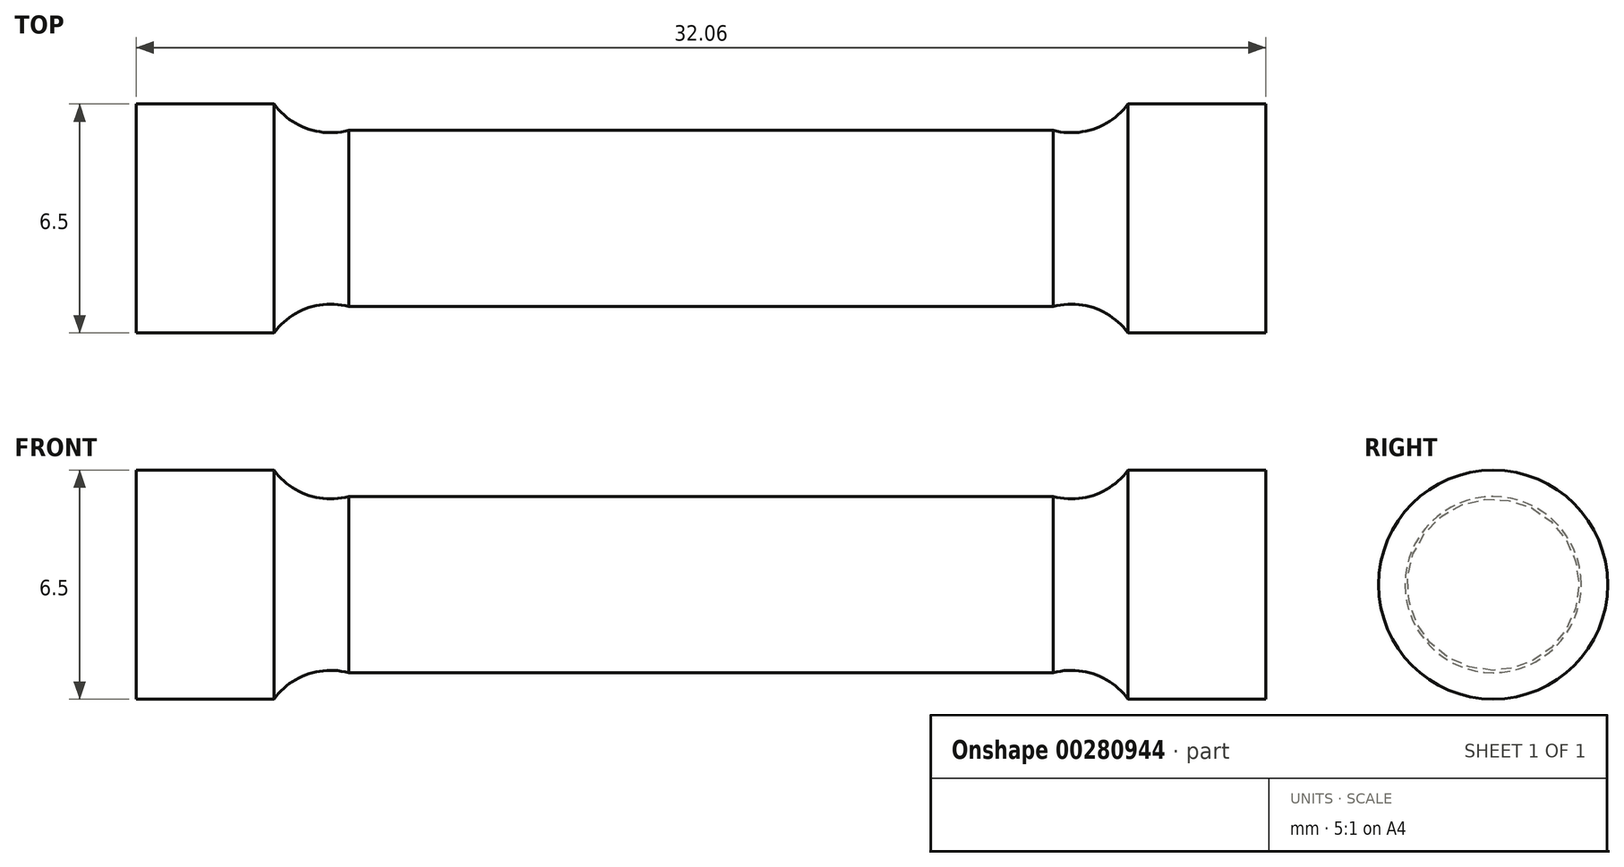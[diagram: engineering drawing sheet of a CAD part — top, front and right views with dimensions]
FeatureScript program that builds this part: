
annotation { "Feature Type Name" : "Feature", "Feature Type Description" : "" }
export const myFeature = defineFeature(function(context is Context, id is Id, definition is map)
    precondition{}
    {
        {
            var Q0;
            Q0=qCreatedBy(makeId("Front.planeOp"),FACE);
            var sketch = newSketch(context, id + "F0", { "sketchPlane" : qUnion([Q0])});
            skLineSegment(sketch, "E0", {"start": v(0, 0) * mm, "end": v(16.03, 0) * mm});
            skLineSegment(sketch, "E1", {"start": v(16.03, 0) * mm, "end": v(16.03, 3.25) * mm});
            skLineSegment(sketch, "E2", {"start": v(16.03, 3.25) * mm, "end": v(12.12, 3.25) * mm});
            skArc(sketch, "E3", {"start": v(10, 2.5) * mm, "mid": v(11.17, 2.55) * mm, "end": v(12.12, 3.25) * mm});
            skLineSegment(sketch, "E4", {"start": v(10, 2.5) * mm, "end": v(0, 2.5) * mm});
            skLineSegment(sketch, "E5.MirrorCS", {"start": v(0, 0) * mm, "end": v(-16.03, 0) * mm});
            skLineSegment(sketch, "E6.MirrorCS", {"start": v(-16.03, 0) * mm, "end": v(-16.03, 3.25) * mm});
            skArc(sketch, "E7.MirrorCS", {"start": v(-10, 2.5) * mm, "mid": v(-11.17, 2.55) * mm, "end": v(-12.12, 3.25) * mm});
            skLineSegment(sketch, "E8.MirrorCS", {"start": v(-10, 2.5) * mm, "end": v(0, 2.5) * mm});
            skLineSegment(sketch, "E9.MirrorCS", {"start": v(-16.03, 3.25) * mm, "end": v(-12.12, 3.25) * mm});
            skSolve(sketch);
        }
        {
            var Q0;
            Q0=makeQuery(id+"F0.imprint","IMPRINT",FACE,{"disambiguationData":[TD([[makeQuery(id+"F0.imprint","IMPRINT",EDGE,{"derivedFrom":sQuery(id+"F0.wireOp",EDGE,"E0")}),1.0]])]});
            var Q1;
            Q1=sQuery(id+"F0.wireOp",EDGE,"E5.MirrorCS");
            revolve(context, id + "F1", {"entities" : qUnion([Q0]), "axis" : qUnion([Q1]), "revolveType" : RevolveType.FULL});
        }
    });
